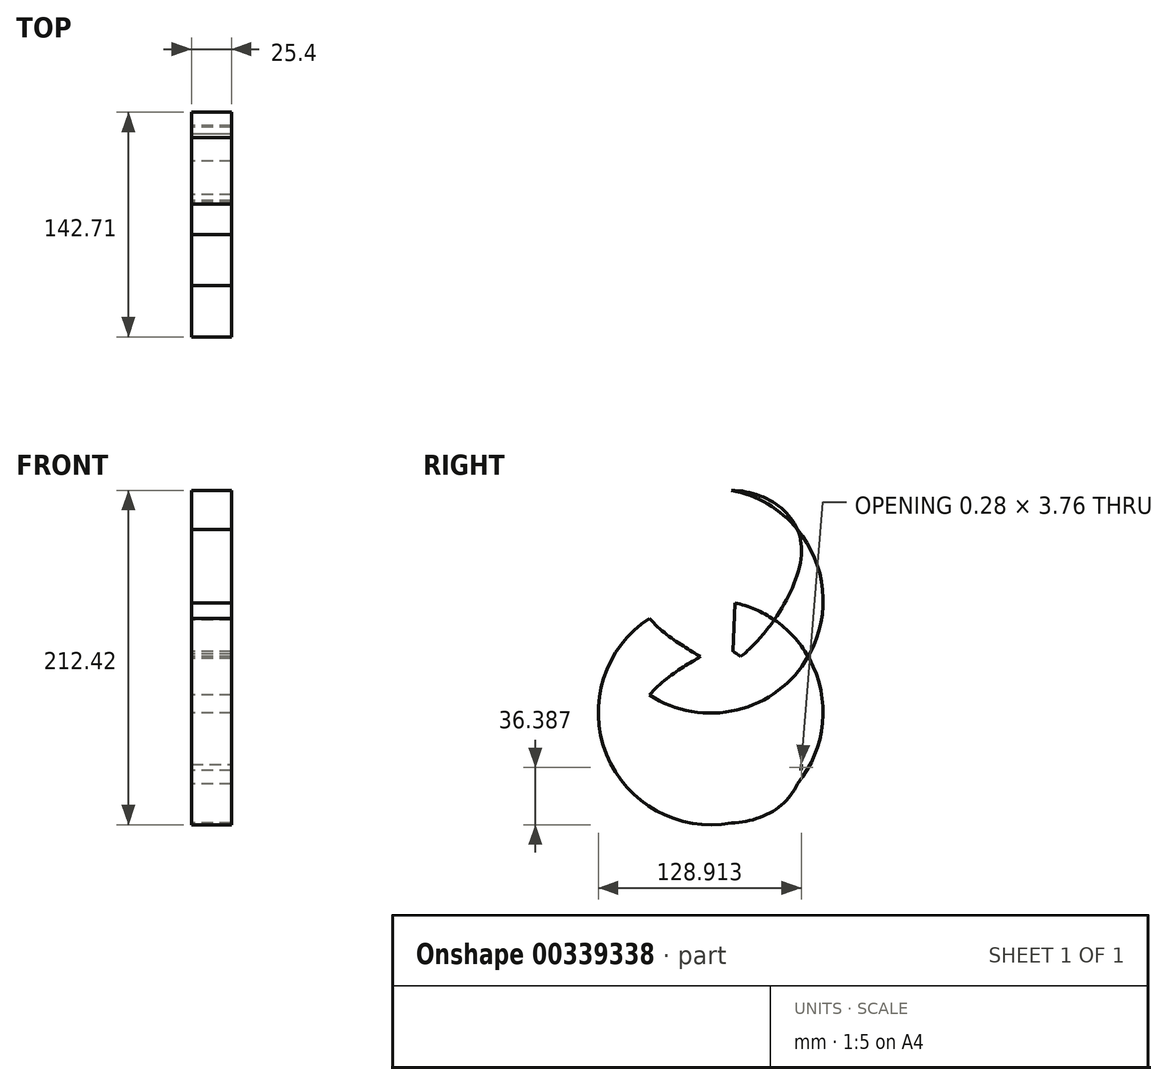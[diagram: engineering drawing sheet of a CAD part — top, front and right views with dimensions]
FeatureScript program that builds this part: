
annotation { "Feature Type Name" : "Feature", "Feature Type Description" : "" }
export const myFeature = defineFeature(function(context is Context, id is Id, definition is map)
    precondition{}
    {
        {
            var Q0;
            Q0=qCreatedBy(makeId("Right.planeOp"),FACE);
            var sketch = newSketch(context, id + "F0", { "sketchPlane" : qUnion([Q0])});
            skLineSegment(sketch, "E0", {"start": v(74.63, 75.15) * mm, "end": v(63.45, -77.1) * mm});
            skLineSegment(sketch, "E1", {"start": v(23.13, 76.67) * mm, "end": v(17.82, -77.1) * mm});
            skFitSpline(sketch, "E2", {"points": [v(20.48, 0) * mm, v(20.65, 4.87) * mm], "startDerivative": vector(0.17, 4.87) * mm, "endDerivative": vector(0.17, 4.87) * mm});
            skFitSpline(sketch, "E3", {"points": [v(0, 0) * mm, v(20.6, 3.25) * mm, v(63.8, -72.31) * mm, v(6.73, -104.1) * mm, v(-40.99, -41.61) * mm, v(0, 0) * mm]});
            skCircle(sketch, "E4", {"center": v(6.38, 35.46) * mm, "radius": 71.35 * mm});
            skPoint(sketch, "E5", {"position": v(22.18, 49) * mm});
            skPoint(sketch, "E6", {"position": v(38.16, 40.97) * mm});
            skPoint(sketch, "E7", {"position": v(45.76, 26.76) * mm});
            skPoint(sketch, "E8", {"position": v(0, 26.44) * mm});
            skCircle(sketch, "E9.MirrorC", {"center": v(6.38, -35.46) * mm, "radius": 71.35 * mm});
            skFitSpline(sketch, "E10.MirrorC", {"points": [v(0, 0) * mm, v(20.6, -3.25) * mm, v(63.8, 72.31) * mm, v(6.73, 104.1) * mm, v(-40.99, 41.61) * mm, v(0, 0) * mm]});
            skSolve(sketch);
        }
        {
            var Q0;
            {var subQ0=sQuery(id+"F0.wireOp",EDGE,"E4");var subQ1=sQuery(id+"F0.wireOp",EDGE,"E0");var subQ2=makeQuery(id+"F0.imprint","INTERSECT",VERTEX,{"disambiguationData":[OD(0.0)],"derivedFrom":[subQ1,subQ0]});Q0=makeQuery(id+"F0.imprint","IMPRINT",FACE,{"disambiguationData":[TD([[makeQuery(id+"F0.imprint","IMPRINT",EDGE,{"disambiguationData":[TD([[subQ2,-1.0]])],"derivedFrom":subQ1}),1.0]])]});}
            var Q1;
            {var subQ0=sQuery(id+"F0.wireOp",EDGE,"E9.MirrorC");var subQ1=sQuery(id+"F0.wireOp",EDGE,"E3");var subQ2=makeQuery(id+"F0.imprint","INTERSECT",VERTEX,{"disambiguationData":[OD(0.0)],"derivedFrom":[subQ1,subQ0]});Q1=makeQuery(id+"F0.imprint","IMPRINT",FACE,{"disambiguationData":[TD([[makeQuery(id+"F0.imprint","IMPRINT",EDGE,{"disambiguationData":[TD([[subQ2,-1.0]])],"derivedFrom":subQ1}),-1.0]])]});}
            var Q2;
            {var subQ0=sQuery(id+"F0.wireOp",EDGE,"E4");var subQ1=sQuery(id+"F0.wireOp",EDGE,"E10.MirrorC");var subQ2=makeQuery(id+"F0.imprint","INTERSECT",VERTEX,{"disambiguationData":[OD(0.0)],"derivedFrom":[subQ1,subQ0]});Q2=makeQuery(id+"F0.imprint","IMPRINT",FACE,{"disambiguationData":[TD([[makeQuery(id+"F0.imprint","IMPRINT",EDGE,{"disambiguationData":[TD([[subQ2,-1.0]])],"derivedFrom":subQ1}),1.0]])]});}
            var Q3;
            {var subQ0=sQuery(id+"F0.wireOp",EDGE,"E4");var subQ1=sQuery(id+"F0.wireOp",EDGE,"E0");var subQ2=makeQuery(id+"F0.imprint","INTERSECT",VERTEX,{"disambiguationData":[OD(1.0)],"derivedFrom":[subQ1,subQ0]});Q3=makeQuery(id+"F0.imprint","IMPRINT",FACE,{"disambiguationData":[TD([[makeQuery(id+"F0.imprint","IMPRINT",EDGE,{"disambiguationData":[TD([[subQ2,-1.0]])],"derivedFrom":subQ1}),-1.0]])]});}
            var Q4;
            {var subQ0=sQuery(id+"F0.wireOp",EDGE,"E9.MirrorC");var subQ1=sQuery(id+"F0.wireOp",EDGE,"E3");var subQ2=makeQuery(id+"F0.imprint","INTERSECT",VERTEX,{"disambiguationData":[OD(1.0)],"derivedFrom":[subQ1,subQ0]});Q4=makeQuery(id+"F0.imprint","IMPRINT",FACE,{"disambiguationData":[TD([[makeQuery(id+"F0.imprint","IMPRINT",EDGE,{"disambiguationData":[TD([[subQ2,-1.0]])],"derivedFrom":subQ1}),1.0]])]});}
            var Q5;
            {var subQ0=sQuery(id+"F0.wireOp",EDGE,"E9.MirrorC");var subQ1=sQuery(id+"F0.wireOp",EDGE,"E0");var subQ2=makeQuery(id+"F0.imprint","INTERSECT",VERTEX,{"derivedFrom":[subQ1,subQ0]});Q5=makeQuery(id+"F0.imprint","IMPRINT",FACE,{"disambiguationData":[TD([[makeQuery(id+"F0.imprint","IMPRINT",EDGE,{"disambiguationData":[TD([[subQ2,-1.0]])],"derivedFrom":subQ1}),1.0]])]});}
            var Q6;
            {var subQ0=sQuery(id+"F0.wireOp",EDGE,"E4");var subQ5=sQuery(id+"F0.wireOp",EDGE,"E0");var subQ8=makeQuery(id+"F0.imprint","INTERSECT",VERTEX,{"disambiguationData":[OD(0.0)],"derivedFrom":[subQ5,subQ0]});Q6=makeQuery(id+"F0.imprint","IMPRINT",FACE,{"disambiguationData":[TD([[makeQuery(id+"F0.imprint","IMPRINT",EDGE,{"disambiguationData":[TD([[subQ8,-1.0]])],"derivedFrom":subQ5}),-1.0]])]});}
            var Q7;
            {var subQ0=sQuery(id+"F0.wireOp",EDGE,"E9.MirrorC");var subQ1=sQuery(id+"F0.wireOp",EDGE,"E0");var subQ2=makeQuery(id+"F0.imprint","INTERSECT",VERTEX,{"derivedFrom":[subQ1,subQ0]});Q7=makeQuery(id+"F0.imprint","IMPRINT",FACE,{"disambiguationData":[TD([[makeQuery(id+"F0.imprint","IMPRINT",EDGE,{"disambiguationData":[TD([[subQ2,-1.0]])],"derivedFrom":subQ1}),-1.0]])]});}
            var Q8;
            {var subQ0=sQuery(id+"F0.wireOp",EDGE,"E10.MirrorC");var subQ1=sQuery(id+"F0.wireOp",EDGE,"E3");var subQ2=makeQuery(id+"F0.imprint","INTERSECT",VERTEX,{"disambiguationData":[OD(0.0)],"derivedFrom":[subQ1,subQ0]});Q8=makeQuery(id+"F0.imprint","IMPRINT",FACE,{"disambiguationData":[TD([[makeQuery(id+"F0.imprint","IMPRINT",EDGE,{"disambiguationData":[TD([[subQ2,1.0]])],"derivedFrom":subQ1}),1.0]])]});}
            var Q9;
            {var subQ3=sQuery(id+"F0.wireOp",EDGE,"E9.MirrorC");var subQ5=makeQuery(id+"F0.imprint","INTERSECT",VERTEX,{"derivedFrom":[sQuery(id+"F0.wireOp",EDGE,"E1"),subQ3]});Q9=makeQuery(id+"F0.imprint","IMPRINT",FACE,{"disambiguationData":[TD([[makeQuery(id+"F0.imprint","IMPRINT",EDGE,{"disambiguationData":[TD([[subQ5,1.0]])],"derivedFrom":subQ3}),1.0]])]});}
            var Q10;
            {var subQ1=sQuery(id+"F0.wireOp",EDGE,"E3");var subQ7=sQuery(id+"F0.wireOp",EDGE,"E0");var subQ8=makeQuery(id+"F0.imprint","INTERSECT",VERTEX,{"disambiguationData":[OD(0.0)],"derivedFrom":[subQ7,subQ1]});Q10=makeQuery(id+"F0.imprint","IMPRINT",FACE,{"disambiguationData":[TD([[makeQuery(id+"F0.imprint","IMPRINT",EDGE,{"disambiguationData":[TD([[subQ8,1.0]])],"derivedFrom":subQ7}),-1.0]])]});}
            var Q11;
            {var subQ0=sQuery(id+"F0.wireOp",EDGE,"E4");var subQ1=sQuery(id+"F0.wireOp",EDGE,"E9.MirrorC");var subQ2=makeQuery(id+"F0.imprint","INTERSECT",VERTEX,{"disambiguationData":[OD(0.0)],"derivedFrom":[subQ1,subQ0]});Q11=makeQuery(id+"F0.imprint","IMPRINT",FACE,{"disambiguationData":[TD([[makeQuery(id+"F0.imprint","IMPRINT",EDGE,{"disambiguationData":[TD([[subQ2,-1.0]])],"derivedFrom":subQ1}),1.0]])]});}
            extrude(context, id + "F1", {"entities" : qUnion([Q0, Q1, Q2, Q3, Q4, Q5, Q6, Q7, Q8, Q9, Q10, Q11]), "depth" : 25.4 * mm});
        }
    });
